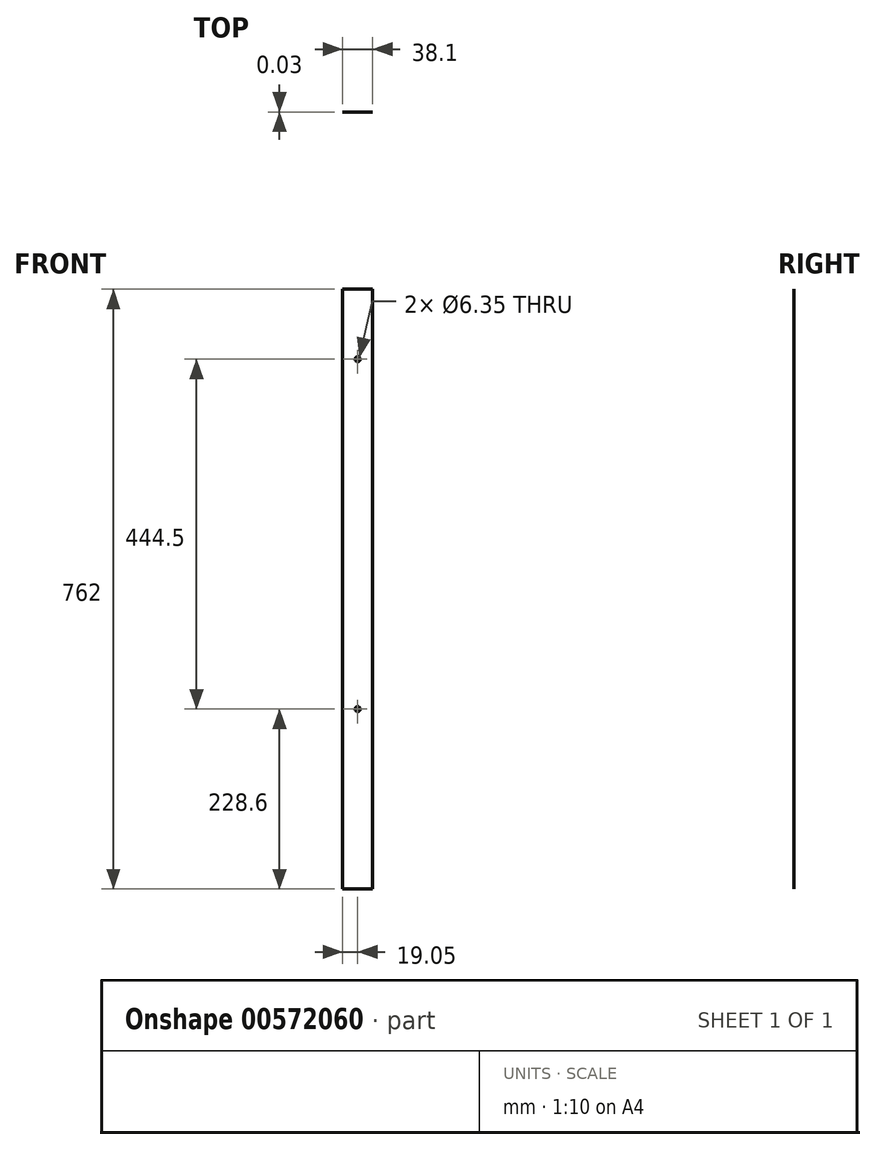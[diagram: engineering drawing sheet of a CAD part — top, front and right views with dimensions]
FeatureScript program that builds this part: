
annotation { "Feature Type Name" : "Feature", "Feature Type Description" : "" }
export const myFeature = defineFeature(function(context is Context, id is Id, definition is map)
    precondition{}
    {
        {
            var Q0;
            Q0=qCreatedBy(makeId("Front.planeOp"),FACE);
            var sketch = newSketch(context, id + "F0", { "sketchPlane" : qUnion([Q0])});
            skLineSegment(sketch, "E0.bottom", {"start": v(19.05, 381) * mm, "end": v(-19.05, 381) * mm});
            skLineSegment(sketch, "E0.top", {"start": v(19.05, -381) * mm, "end": v(-19.05, -381) * mm});
            skLineSegment(sketch, "E0.left", {"start": v(19.05, 381) * mm, "end": v(19.05, -381) * mm});
            skLineSegment(sketch, "E0.right", {"start": v(-19.05, 381) * mm, "end": v(-19.05, -381) * mm});
            skPoint(sketch, "E0.middle", {"position": v(0, 0) * mm});
            skSolve(sketch);
        }
        {
            var Q0;
            Q0=makeQuery(id+"F0.imprint","IMPRINT",FACE,{"disambiguationData":[TD([[makeQuery(id+"F0.imprint","IMPRINT",EDGE,{"derivedFrom":sQuery(id+"F0.wireOp",EDGE,"E0.bottom")}),1.0]])]});
            extrude(context, id + "F1", {"entities" : qUnion([Q0]), "depth" : 0.03 * mm, "offsetDistance" : 25.4 * mm});
        }
        {
            var Q0;
            Q0=makeQuery(id+"F1.opExtrude","CAP_FACE",FACE,{"disambiguationData":[OSD([sQuery(id+"F0.wireOp",EDGE,"E0.bottom"),sQuery(id+"F0.wireOp",EDGE,"E0.top"),sQuery(id+"F0.wireOp",EDGE,"E0.left"),sQuery(id+"F0.wireOp",EDGE,"E0.right")])],"isStart":false});
            var sketch = newSketch(context, id + "F2", { "sketchPlane" : qUnion([Q0])});
            skPoint(sketch, "E1", {"position": v(0, 292.1) * mm});
            skPoint(sketch, "E2", {"position": v(0, -152.4) * mm});
            skSolve(sketch);
        }
        {
            var Q0;
            Q0=sQuery(id+"F2.wireOp",VERTEX,"E1");
            var Q1;
            Q1=sQuery(id+"F2.wireOp",VERTEX,"E2");
            var Q2;
            Q2=makeQuery(id+"F1.opExtrude","SWEPT_BODY",BODY,{"disambiguationData":[OSD([sQuery(id+"F0.wireOp",EDGE,"E0.bottom"),sQuery(id+"F0.wireOp",EDGE,"E0.top"),sQuery(id+"F0.wireOp",EDGE,"E0.left"),sQuery(id+"F0.wireOp",EDGE,"E0.right")])]});
            hole(context, id + "F3", {"style" : HoleStyle.SIMPLE, "endStyle" : HoleEndStyle.THROUGH, "holeDiameter" : 6.35 * mm, "majorDiameter" : 6.35 * mm, "isTappedThrough" : true, "tappedDepth" : 12.7 * mm, "tapClearance" : 3, "locations" : qUnion([Q0, Q1]), "scope" : qUnion([Q2])});
        }
    });
